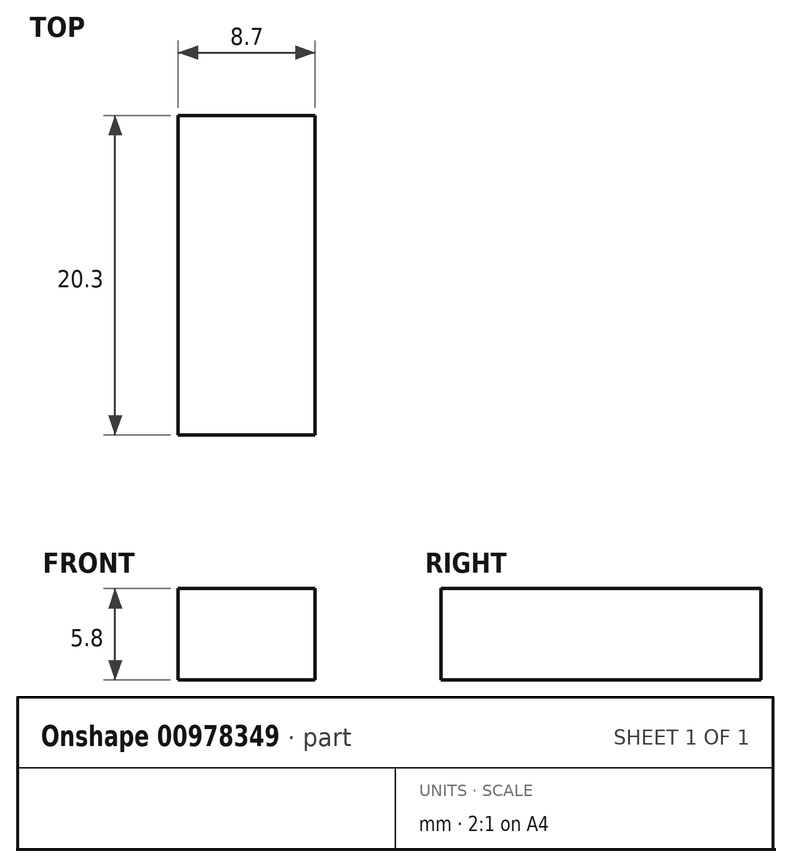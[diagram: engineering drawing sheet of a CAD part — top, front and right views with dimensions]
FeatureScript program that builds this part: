
annotation { "Feature Type Name" : "Feature", "Feature Type Description" : "" }
export const myFeature = defineFeature(function(context is Context, id is Id, definition is map)
    precondition{}
    {
        {
            var Q0;
            Q0=qCreatedBy(makeId("Front.planeOp"),FACE);
            var sketch = newSketch(context, id + "F0", { "sketchPlane" : qUnion([Q0])});
            skLineSegment(sketch, "E0.bottom", {"start": v(4.35, 2.9) * mm, "end": v(-4.35, 2.9) * mm});
            skLineSegment(sketch, "E0.top", {"start": v(4.35, -2.9) * mm, "end": v(-4.35, -2.9) * mm});
            skLineSegment(sketch, "E0.left", {"start": v(4.35, 2.9) * mm, "end": v(4.35, -2.9) * mm});
            skLineSegment(sketch, "E0.right", {"start": v(-4.35, 2.9) * mm, "end": v(-4.35, -2.9) * mm});
            skPoint(sketch, "E0.middle", {"position": v(0, 0) * mm});
            skSolve(sketch);
        }
        {
            var Q0;
            Q0=makeQuery(id+"F0.imprint","IMPRINT",FACE,{"disambiguationData":[TD([[makeQuery(id+"F0.imprint","IMPRINT",EDGE,{"derivedFrom":sQuery(id+"F0.wireOp",EDGE,"E0.bottom")}),1.0]])]});
            extrude(context, id + "F1", {"entities" : qUnion([Q0]), "depth" : (5.8 * 3.5) * mm, "offsetDistance" : 25 * mm});
        }
    });
